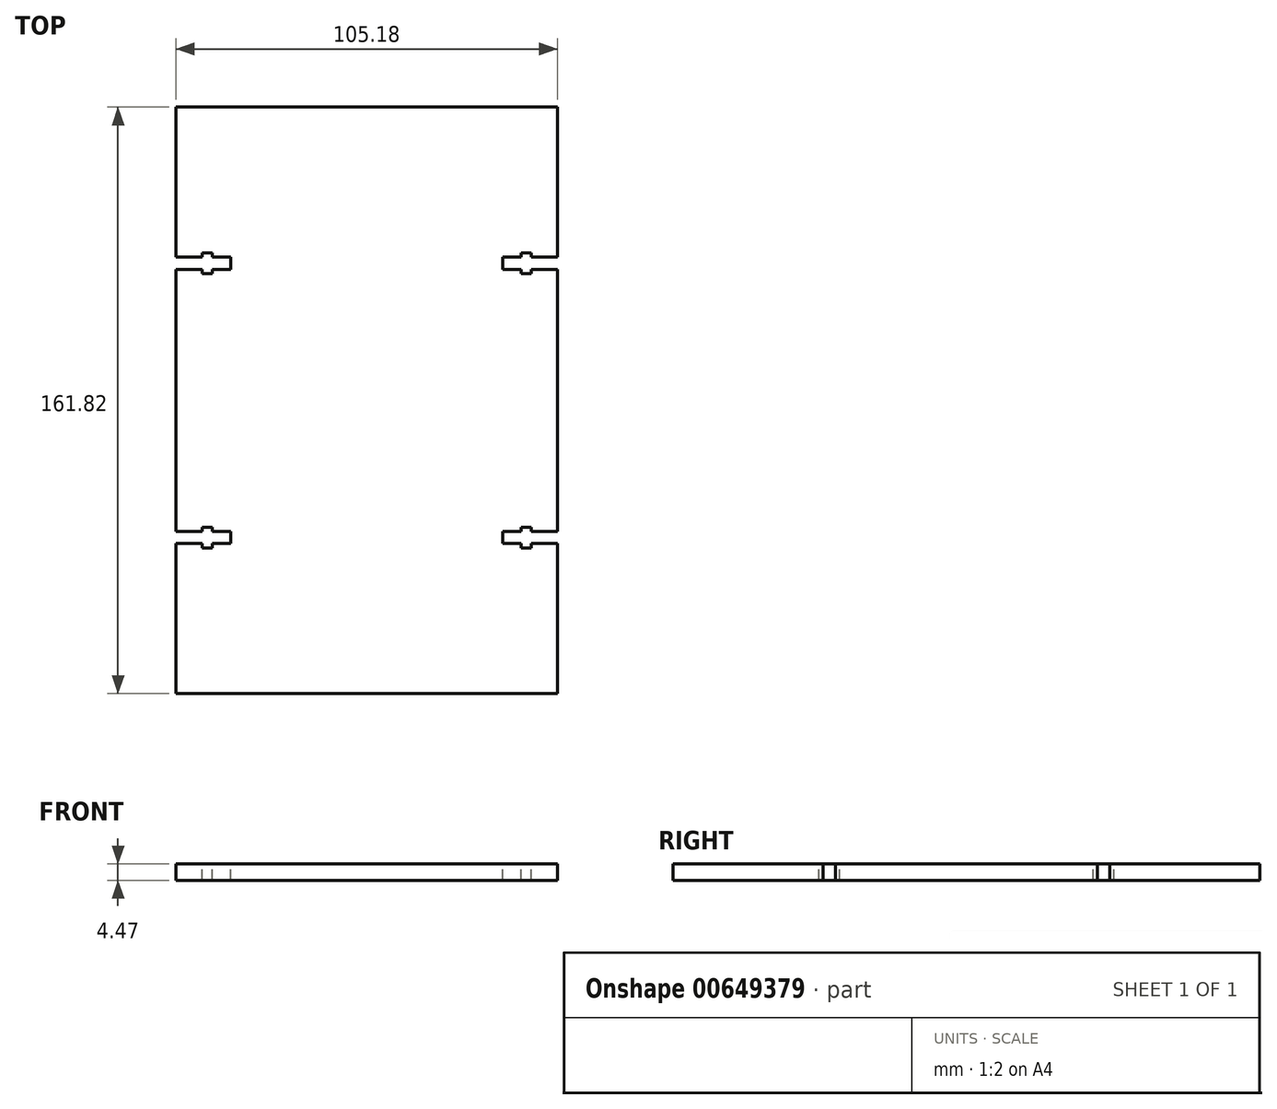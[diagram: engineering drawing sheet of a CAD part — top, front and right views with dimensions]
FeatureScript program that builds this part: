
annotation { "Feature Type Name" : "Feature", "Feature Type Description" : "" }
export const myFeature = defineFeature(function(context is Context, id is Id, definition is map)
    precondition{}
    {
        {
            var Q0;
            Q0=qCreatedBy(makeId("Top.planeOp"),FACE);
            var sketch = newSketch(context, id + "F0", { "sketchPlane" : qUnion([Q0])});
            skLineSegment(sketch, "E0.bottom", {"start": v(-52.6, 80.91) * mm, "end": v(52.6, 80.91) * mm});
            skLineSegment(sketch, "E0.top", {"start": v(-52.6, -80.91) * mm, "end": v(52.6, -80.91) * mm});
            skLineSegment(sketch, "E0.left", {"start": v(-52.6, 80.91) * mm, "end": v(-52.6, -80.91) * mm});
            skLineSegment(sketch, "E0.right", {"start": v(52.6, 80.91) * mm, "end": v(52.6, -80.91) * mm});
            skSolve(sketch);
        }
        {
            var Q0;
            Q0 = qSketchRegion(id + "F0", true);
            extrude(context, id + "F1", {"entities" : qUnion([Q0]), "depth" : 4.47 * mm, "offsetDistance" : 25.4 * mm});
        }
        {
            var Q0;
            Q0=makeQuery(id+"F1.opExtrude","CAP_FACE",FACE,{"disambiguationData":[OSD([sQuery(id+"F0.wireOp",EDGE,"E0.bottom"),sQuery(id+"F0.wireOp",EDGE,"E0.top"),sQuery(id+"F0.wireOp",EDGE,"E0.left"),sQuery(id+"F0.wireOp",EDGE,"E0.right")])],"isStart":false});
            var sketch = newSketch(context, id + "F2", { "sketchPlane" : qUnion([Q0])});
            skLineSegment(sketch, "E1", {"start": v(-52.6, 39.5) * mm, "end": v(-45.45, 39.5) * mm});
            skLineSegment(sketch, "E2", {"start": v(-45.45, 39.5) * mm, "end": v(-45.45, 40.7) * mm});
            skLineSegment(sketch, "E3", {"start": v(-45.45, 40.7) * mm, "end": v(-42.66, 40.7) * mm});
            skLineSegment(sketch, "E4", {"start": v(-42.66, 40.7) * mm, "end": v(-42.66, 39.5) * mm});
            skLineSegment(sketch, "E5", {"start": v(-42.66, 39.5) * mm, "end": v(-37.53, 39.5) * mm});
            skLineSegment(sketch, "E6", {"start": v(-37.53, 39.5) * mm, "end": v(-37.53, 36.16) * mm});
            skLineSegment(sketch, "E7", {"start": v(-37.53, 36.16) * mm, "end": v(-42.66, 36.16) * mm});
            skLineSegment(sketch, "E8", {"start": v(-42.66, 36.16) * mm, "end": v(-42.66, 34.98) * mm});
            skLineSegment(sketch, "E9", {"start": v(-42.66, 34.98) * mm, "end": v(-45.45, 34.98) * mm});
            skLineSegment(sketch, "E10", {"start": v(-45.45, 34.98) * mm, "end": v(-45.45, 36.16) * mm});
            skLineSegment(sketch, "E11", {"start": v(-45.45, 36.16) * mm, "end": v(-52.6, 36.16) * mm});
            skLineSegment(sketch, "E12", {"start": v(-52.6, 36.16) * mm, "end": v(-52.6, 39.5) * mm});
            skLineSegment(sketch, "E13", {"start": v(-52.6, 37.83) * mm, "end": v(-25.97, 37.83) * mm, "construction": true});
            skLineSegment(sketch, "E14.MirrorCS", {"start": v(-45.45, 40.7) * mm, "end": v(-45.45, 39.5) * mm});
            skLineSegment(sketch, "E15.MirrorCS", {"start": v(-42.66, 34.98) * mm, "end": v(-42.66, 36.16) * mm});
            skLineSegment(sketch, "E16.MirrorCS", {"start": v(-37.53, 36.16) * mm, "end": v(-37.53, 39.5) * mm});
            skLineSegment(sketch, "E17.MirrorCS", {"start": v(-42.66, 39.5) * mm, "end": v(-42.66, 40.7) * mm});
            skLineSegment(sketch, "E18.MirrorCS", {"start": v(-42.66, 40.7) * mm, "end": v(-45.45, 40.7) * mm});
            skLineSegment(sketch, "E19.MirrorCS", {"start": v(-45.45, 34.98) * mm, "end": v(-42.66, 34.98) * mm});
            skLineSegment(sketch, "E20.MirrorCS", {"start": v(-52.6, 39.5) * mm, "end": v(-52.6, 36.16) * mm});
            skLineSegment(sketch, "E21.MirrorCS", {"start": v(-45.45, 36.16) * mm, "end": v(-45.45, 34.98) * mm});
            skLineSegment(sketch, "E22.MirrorCS", {"start": v(-42.66, 36.16) * mm, "end": v(-37.53, 36.16) * mm});
            skLineSegment(sketch, "E23.MirrorCS", {"start": v(-52.6, 36.16) * mm, "end": v(-45.45, 36.16) * mm});
            skLineSegment(sketch, "E24.MirrorCS", {"start": v(-45.45, 39.5) * mm, "end": v(-52.6, 39.5) * mm});
            skLineSegment(sketch, "E25.MirrorCS", {"start": v(-37.53, 39.5) * mm, "end": v(-42.66, 39.5) * mm});
            skLineSegment(sketch, "E26.MirrorCS", {"start": v(-45.45, -40.7) * mm, "end": v(-45.45, -39.5) * mm});
            skLineSegment(sketch, "E27.MirrorCS", {"start": v(-45.45, -34.98) * mm, "end": v(-45.45, -36.16) * mm});
            skLineSegment(sketch, "E28.MirrorCS", {"start": v(-42.66, -36.16) * mm, "end": v(-42.66, -34.98) * mm});
            skLineSegment(sketch, "E29.MirrorCS", {"start": v(-42.66, -39.5) * mm, "end": v(-42.66, -40.7) * mm});
            skLineSegment(sketch, "E30.MirrorCS", {"start": v(-42.66, -40.7) * mm, "end": v(-42.66, -39.5) * mm});
            skLineSegment(sketch, "E31.MirrorCS", {"start": v(-45.45, -39.5) * mm, "end": v(-45.45, -40.7) * mm});
            skLineSegment(sketch, "E32.MirrorCS", {"start": v(-42.66, -34.98) * mm, "end": v(-42.66, -36.16) * mm});
            skLineSegment(sketch, "E33.MirrorCS", {"start": v(-45.45, -36.16) * mm, "end": v(-45.45, -34.98) * mm});
            skLineSegment(sketch, "E34.MirrorCS", {"start": v(-37.53, -36.16) * mm, "end": v(-37.53, -39.5) * mm});
            skLineSegment(sketch, "E35.MirrorCS", {"start": v(-42.66, -40.7) * mm, "end": v(-45.45, -40.7) * mm});
            skLineSegment(sketch, "E36.MirrorCS", {"start": v(-37.53, -39.5) * mm, "end": v(-42.66, -39.5) * mm});
            skLineSegment(sketch, "E37.MirrorCS", {"start": v(-42.66, -34.98) * mm, "end": v(-45.45, -34.98) * mm});
            skLineSegment(sketch, "E38.MirrorCS", {"start": v(-42.66, -36.16) * mm, "end": v(-37.53, -36.16) * mm});
            skLineSegment(sketch, "E39.MirrorCS", {"start": v(-45.45, -36.16) * mm, "end": v(-52.6, -36.16) * mm});
            skLineSegment(sketch, "E40.MirrorCS", {"start": v(-52.6, -36.16) * mm, "end": v(-52.6, -39.5) * mm});
            skLineSegment(sketch, "E41.MirrorCS", {"start": v(-45.45, -39.5) * mm, "end": v(-52.6, -39.5) * mm});
            skLineSegment(sketch, "E42.MirrorCS", {"start": v(-37.53, -36.16) * mm, "end": v(-42.66, -36.16) * mm});
            skLineSegment(sketch, "E43.MirrorCS", {"start": v(-37.53, -39.5) * mm, "end": v(-37.53, -36.16) * mm});
            skLineSegment(sketch, "E44.MirrorCS", {"start": v(-42.66, -39.5) * mm, "end": v(-37.53, -39.5) * mm});
            skLineSegment(sketch, "E45.MirrorCS", {"start": v(-45.45, -40.7) * mm, "end": v(-42.66, -40.7) * mm});
            skLineSegment(sketch, "E46.MirrorCS", {"start": v(-52.6, -39.5) * mm, "end": v(-45.45, -39.5) * mm});
            skLineSegment(sketch, "E47.MirrorCS", {"start": v(-52.6, -39.5) * mm, "end": v(-52.6, -36.16) * mm});
            skLineSegment(sketch, "E48.MirrorCS", {"start": v(-45.45, -34.98) * mm, "end": v(-42.66, -34.98) * mm});
            skLineSegment(sketch, "E49.MirrorCS", {"start": v(-52.6, -36.16) * mm, "end": v(-45.45, -36.16) * mm});
            skLineSegment(sketch, "E50.MirrorCS", {"start": v(42.66, 39.5) * mm, "end": v(42.66, 40.7) * mm});
            skLineSegment(sketch, "E51.MirrorCS", {"start": v(52.6, 36.16) * mm, "end": v(52.6, 39.5) * mm});
            skLineSegment(sketch, "E52.MirrorCS", {"start": v(42.66, 34.98) * mm, "end": v(45.45, 34.98) * mm});
            skLineSegment(sketch, "E53.MirrorCS", {"start": v(42.66, 40.7) * mm, "end": v(42.66, 39.5) * mm});
            skLineSegment(sketch, "E54.MirrorCS", {"start": v(37.53, 36.16) * mm, "end": v(37.53, 39.5) * mm});
            skLineSegment(sketch, "E55.MirrorCS", {"start": v(45.45, -40.7) * mm, "end": v(42.66, -40.7) * mm});
            skLineSegment(sketch, "E56.MirrorCS", {"start": v(45.45, -39.5) * mm, "end": v(45.45, -40.7) * mm});
            skLineSegment(sketch, "E57.MirrorCS", {"start": v(42.66, -36.16) * mm, "end": v(42.66, -34.98) * mm});
            skLineSegment(sketch, "E58.MirrorCS", {"start": v(37.53, -36.16) * mm, "end": v(37.53, -39.5) * mm});
            skLineSegment(sketch, "E59.MirrorCS", {"start": v(52.6, -36.16) * mm, "end": v(52.6, -39.5) * mm});
            skLineSegment(sketch, "E60.MirrorCS", {"start": v(45.45, -36.16) * mm, "end": v(45.45, -34.98) * mm});
            skLineSegment(sketch, "E61.MirrorCS", {"start": v(42.66, 40.7) * mm, "end": v(45.45, 40.7) * mm});
            skLineSegment(sketch, "E62.MirrorCS", {"start": v(45.45, 36.16) * mm, "end": v(45.45, 34.98) * mm});
            skLineSegment(sketch, "E63.MirrorCS", {"start": v(42.66, -34.98) * mm, "end": v(45.45, -34.98) * mm});
            skLineSegment(sketch, "E64.MirrorCS", {"start": v(42.66, 34.98) * mm, "end": v(42.66, 36.16) * mm});
            skLineSegment(sketch, "E65.MirrorCS", {"start": v(42.66, -40.7) * mm, "end": v(42.66, -39.5) * mm});
            skLineSegment(sketch, "E66.MirrorCS", {"start": v(45.45, 40.7) * mm, "end": v(45.45, 39.5) * mm});
            skLineSegment(sketch, "E67.MirrorCS", {"start": v(52.6, 39.5) * mm, "end": v(52.6, 36.16) * mm});
            skLineSegment(sketch, "E68.MirrorCS", {"start": v(45.45, -34.98) * mm, "end": v(45.45, -36.16) * mm});
            skLineSegment(sketch, "E69.MirrorCS", {"start": v(37.53, -39.5) * mm, "end": v(37.53, -36.16) * mm});
            skLineSegment(sketch, "E70.MirrorCS", {"start": v(45.45, 34.98) * mm, "end": v(42.66, 34.98) * mm});
            skLineSegment(sketch, "E71.MirrorCS", {"start": v(42.66, -40.7) * mm, "end": v(45.45, -40.7) * mm});
            skLineSegment(sketch, "E72.MirrorCS", {"start": v(45.45, -34.98) * mm, "end": v(42.66, -34.98) * mm});
            skLineSegment(sketch, "E73.MirrorCS", {"start": v(42.66, -34.98) * mm, "end": v(42.66, -36.16) * mm});
            skLineSegment(sketch, "E74.MirrorCS", {"start": v(45.45, -40.7) * mm, "end": v(45.45, -39.5) * mm});
            skLineSegment(sketch, "E75.MirrorCS", {"start": v(45.45, 34.98) * mm, "end": v(45.45, 36.16) * mm});
            skLineSegment(sketch, "E76.MirrorCS", {"start": v(42.66, 36.16) * mm, "end": v(42.66, 34.98) * mm});
            skLineSegment(sketch, "E77.MirrorCS", {"start": v(37.53, 39.5) * mm, "end": v(37.53, 36.16) * mm});
            skLineSegment(sketch, "E78.MirrorCS", {"start": v(45.45, 40.7) * mm, "end": v(42.66, 40.7) * mm});
            skLineSegment(sketch, "E79.MirrorCS", {"start": v(45.45, 39.5) * mm, "end": v(45.45, 40.7) * mm});
            skLineSegment(sketch, "E80.MirrorCS", {"start": v(42.66, -39.5) * mm, "end": v(42.66, -40.7) * mm});
            skLineSegment(sketch, "E81.MirrorCS", {"start": v(52.6, -39.5) * mm, "end": v(52.6, -36.16) * mm});
            skLineSegment(sketch, "E82.MirrorCS", {"start": v(45.45, 36.16) * mm, "end": v(52.6, 36.16) * mm});
            skLineSegment(sketch, "E83.MirrorCS", {"start": v(37.53, 39.5) * mm, "end": v(42.66, 39.5) * mm});
            skLineSegment(sketch, "E84.MirrorCS", {"start": v(42.66, -36.16) * mm, "end": v(37.53, -36.16) * mm});
            skLineSegment(sketch, "E85.MirrorCS", {"start": v(52.6, -36.16) * mm, "end": v(45.45, -36.16) * mm});
            skLineSegment(sketch, "E86.MirrorCS", {"start": v(42.66, -39.5) * mm, "end": v(37.53, -39.5) * mm});
            skLineSegment(sketch, "E87.MirrorCS", {"start": v(42.66, 36.16) * mm, "end": v(37.53, 36.16) * mm});
            skLineSegment(sketch, "E88.MirrorCS", {"start": v(45.45, 39.5) * mm, "end": v(52.6, 39.5) * mm});
            skLineSegment(sketch, "E89.MirrorCS", {"start": v(52.6, -39.5) * mm, "end": v(45.45, -39.5) * mm});
            skLineSegment(sketch, "E90.MirrorCS", {"start": v(37.53, -39.5) * mm, "end": v(42.66, -39.5) * mm});
            skLineSegment(sketch, "E91.MirrorCS", {"start": v(52.6, 36.16) * mm, "end": v(45.45, 36.16) * mm});
            skLineSegment(sketch, "E92.MirrorCS", {"start": v(45.45, -36.16) * mm, "end": v(52.6, -36.16) * mm});
            skLineSegment(sketch, "E93.MirrorCS", {"start": v(37.53, -36.16) * mm, "end": v(42.66, -36.16) * mm});
            skLineSegment(sketch, "E94.MirrorCS", {"start": v(37.53, 36.16) * mm, "end": v(42.66, 36.16) * mm});
            skLineSegment(sketch, "E95.MirrorCS", {"start": v(42.66, 39.5) * mm, "end": v(37.53, 39.5) * mm});
            skLineSegment(sketch, "E96.MirrorCS", {"start": v(45.45, -39.5) * mm, "end": v(52.6, -39.5) * mm});
            skLineSegment(sketch, "E97.MirrorCS", {"start": v(52.6, 39.5) * mm, "end": v(45.45, 39.5) * mm});
            skSolve(sketch);
        }
        {
            var Q0;
            Q0 = qSketchRegion(id + "F2", true);
            extrude(context, id + "F3", {"entities" : qUnion([Q0]), "operationType" : NewBodyOperationType.REMOVE, "endBound" : BoundingType.UP_TO_NEXT, "oppositeDirection" : true, "depth" : 25.4 * mm, "offsetDistance" : 25.4 * mm});
        }
    });
